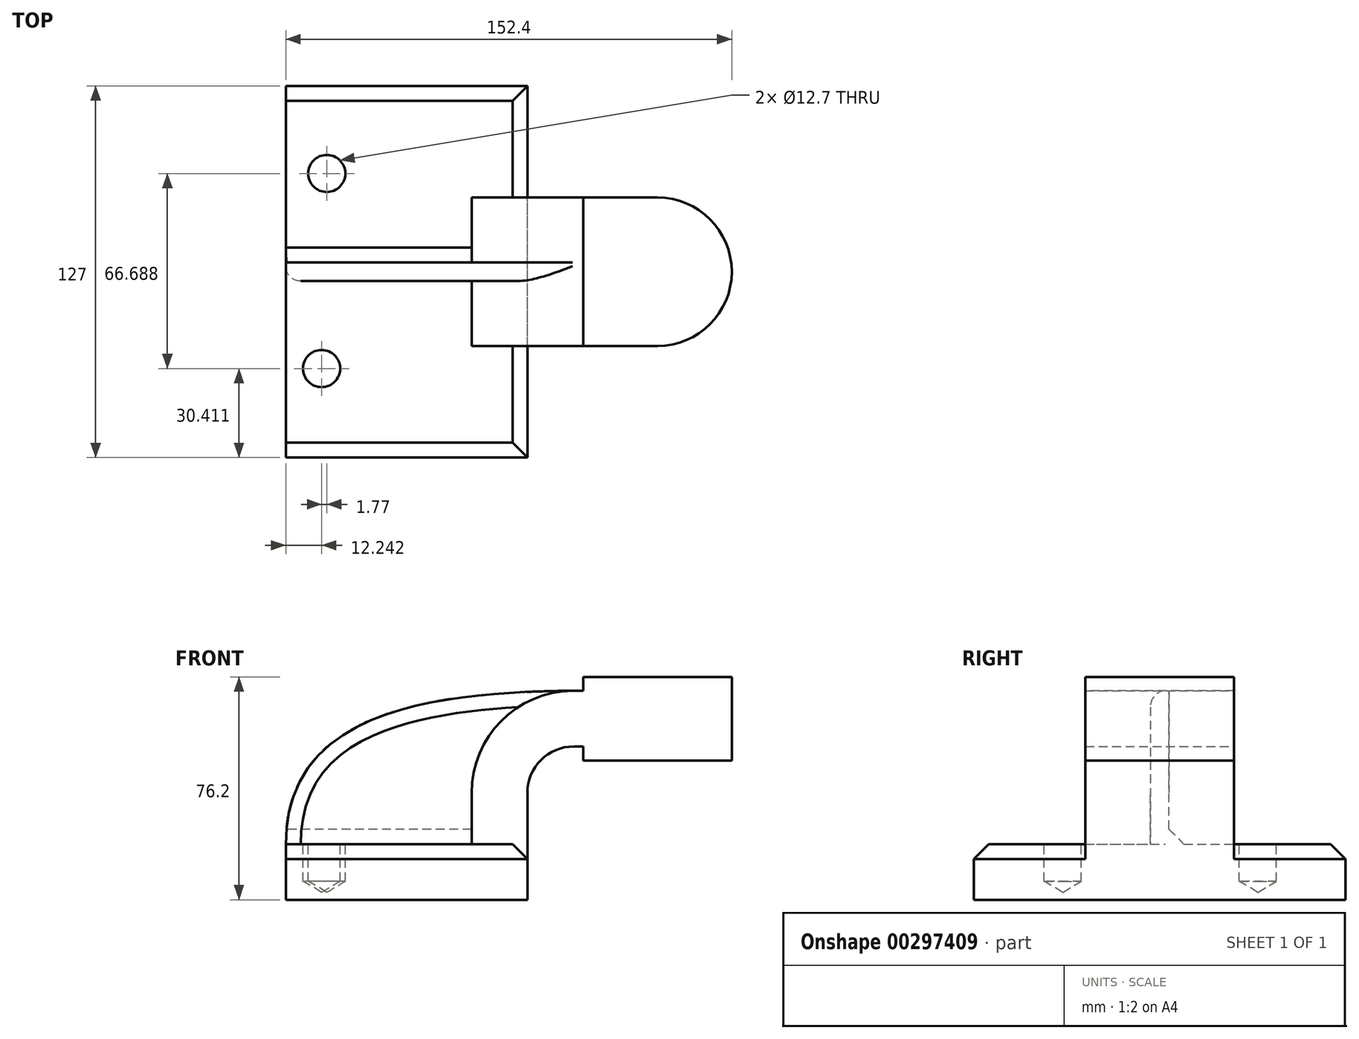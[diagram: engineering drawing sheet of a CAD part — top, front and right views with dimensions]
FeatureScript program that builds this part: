
annotation { "Feature Type Name" : "Feature", "Feature Type Description" : "" }
export const myFeature = defineFeature(function(context is Context, id is Id, definition is map)
    precondition{}
    {
        {
            var Q0;
            Q0=qCreatedBy(makeId("Front.planeOp"),FACE);
            var sketch = newSketch(context, id + "F0", { "sketchPlane" : qUnion([Q0])});
            skLineSegment(sketch, "E0.bottom", {"start": v(41.28, -9.53) * mm, "end": v(-41.27, -9.53) * mm});
            skLineSegment(sketch, "E0.top", {"start": v(41.28, 9.52) * mm, "end": v(-41.28, 9.52) * mm});
            skLineSegment(sketch, "E0.left", {"start": v(41.28, -9.53) * mm, "end": v(41.28, 9.52) * mm});
            skLineSegment(sketch, "E0.right", {"start": v(-41.27, -9.53) * mm, "end": v(-41.27, 9.52) * mm});
            skPoint(sketch, "E0.middle", {"position": v(0, 0) * mm});
            skLineSegment(sketch, "E1.bottom", {"start": v(111.12, 38.1) * mm, "end": v(60.33, 38.1) * mm});
            skLineSegment(sketch, "E1.top", {"start": v(111.12, 66.67) * mm, "end": v(60.33, 66.67) * mm});
            skLineSegment(sketch, "E1.left", {"start": v(111.12, 38.1) * mm, "end": v(111.12, 66.67) * mm});
            skLineSegment(sketch, "E1.right", {"start": v(60.33, 38.1) * mm, "end": v(60.33, 66.67) * mm});
            skPoint(sketch, "E1.middle", {"position": v(85.72, 52.39) * mm});
            skLineSegment(sketch, "E2", {"start": v(41.28, 9.52) * mm, "end": v(41.28, 27) * mm});
            skArc(sketch, "E3", {"start": v(41.28, 27) * mm, "mid": v(45.92, 38.23) * mm, "end": v(57.15, 42.88) * mm});
            skLineSegment(sketch, "E4", {"start": v(57.15, 42.88) * mm, "end": v(85.73, 42.88) * mm});
            skLineSegment(sketch, "E5.0", {"start": v(57.15, 61.93) * mm, "end": v(85.73, 61.93) * mm});
            skArc(sketch, "E5.1", {"start": v(22.23, 27) * mm, "mid": v(32.45, 51.7) * mm, "end": v(57.15, 61.93) * mm});
            skLineSegment(sketch, "E5.2", {"start": v(22.23, 9.52) * mm, "end": v(22.23, 27) * mm});
            skLineSegment(sketch, "E6", {"start": v(85.72, 38.1) * mm, "end": v(85.72, 66.67) * mm});
            skFitSpline(sketch, "E7", {"points": [v(-41.27, 9.52) * mm, v(57.15, 61.93) * mm], "startDerivative": vector(0.8, 125.85) * mm, "endDerivative": vector(171.45, 1.14) * mm});
            skSolve(sketch);
        }
        {
            var Q0;
            Q0=makeQuery(id+"F0.imprint","IMPRINT",FACE,{"disambiguationData":[TD([[makeQuery(id+"F0.imprint","IMPRINT",EDGE,{"derivedFrom":sQuery(id+"F0.wireOp",EDGE,"E0.bottom")}),-1.0]])]});
            extrude(context, id + "F1", {"entities" : qUnion([Q0]), "endBound" : BoundingType.SYMMETRIC, "depth" : 127 * mm});
        }
        {
            var Q0;
            {var subQ1=sQuery(id+"F0.wireOp",EDGE,"E2");Q0=makeQuery(id+"F0.imprint","IMPRINT",FACE,{"disambiguationData":[TD([[makeQuery(id+"F0.imprint","IMPRINT",EDGE,{"derivedFrom":subQ1}),1.0]])]});}
            var Q1;
            {var subQ0=sQuery(id+"F0.wireOp",EDGE,"E4");var subQ1=sQuery(id+"F0.wireOp",EDGE,"E1.right");var subQ2=makeQuery(id+"F0.imprint","INTERSECT",VERTEX,{"derivedFrom":[subQ1,subQ0]});Q1=makeQuery(id+"F0.imprint","IMPRINT",FACE,{"disambiguationData":[TD([[makeQuery(id+"F0.imprint","IMPRINT",EDGE,{"disambiguationData":[TD([[subQ2,-1.0]])],"derivedFrom":subQ1}),-1.0]])]});}
            var Q2;
            {var subQ0=sQuery(id+"F0.wireOp",EDGE,"E1.right");var subQ1=sQuery(id+"F0.wireOp",EDGE,"E1.top");var subQ2=makeQuery(id+"F0.imprint","INTERSECT",VERTEX,{"derivedFrom":[subQ1,subQ0]});Q2=makeQuery(id+"F0.imprint","IMPRINT",FACE,{"disambiguationData":[TD([[makeQuery(id+"F0.imprint","IMPRINT",EDGE,{"disambiguationData":[TD([[subQ2,1.0]])],"derivedFrom":subQ1}),1.0]])]});}
            var Q3;
            {var subQ0=sQuery(id+"F0.wireOp",EDGE,"E1.right");var subQ1=sQuery(id+"F0.wireOp",EDGE,"E1.bottom");var subQ2=makeQuery(id+"F0.imprint","INTERSECT",VERTEX,{"derivedFrom":[subQ1,subQ0]});Q3=makeQuery(id+"F0.imprint","IMPRINT",FACE,{"disambiguationData":[TD([[makeQuery(id+"F0.imprint","IMPRINT",EDGE,{"disambiguationData":[TD([[subQ2,1.0]])],"derivedFrom":subQ1}),-1.0]])]});}
            extrude(context, id + "F2", {"entities" : qUnion([Q0, Q1, Q2, Q3]), "operationType" : NewBodyOperationType.ADD, "endBound" : BoundingType.SYMMETRIC, "depth" : 50.8 * mm});
        }
        {
            var Q0;
            {var subQ3=sQuery(id+"F0.wireOp",EDGE,"E5.2");Q0=makeQuery(id+"F0.imprint","IMPRINT",FACE,{"disambiguationData":[TD([[makeQuery(id+"F0.imprint","IMPRINT",EDGE,{"derivedFrom":subQ3}),1.0]])]});}
            extrude(context, id + "F3", {"entities" : qUnion([Q0]), "operationType" : NewBodyOperationType.ADD, "endBound" : BoundingType.SYMMETRIC, "depth" : 6.35 * mm});
        }
        {
            var Q0;
            {var subQ0=sQuery(id+"F0.wireOp",EDGE,"E1.left");Q0=makeQuery(id+"F0.imprint","IMPRINT",FACE,{"disambiguationData":[TD([[makeQuery(id+"F0.imprint","IMPRINT",EDGE,{"derivedFrom":subQ0}),1.0]])]});}
            var Q1;
            Q1=sQuery(id+"F0.wireOp",EDGE,"E6");
            revolve(context, id + "F4", {"operationType" : NewBodyOperationType.ADD, "entities" : qUnion([Q0]), "axis" : qUnion([Q1]), "revolveType" : RevolveType.FULL});
        }
        {
            var Q0;
            Q0=makeQuery(id+"F3.opExtrude","CAP_EDGE",EDGE,{"disambiguationData":[OSD([sQuery(id+"F0.wireOp",EDGE,"E0.top")])],"isStart":false});
            var Q1;
            Q1=makeQuery(id+"F3.opExtrude","CAP_EDGE",EDGE,{"disambiguationData":[OSD([sQuery(id+"F0.wireOp",EDGE,"E0.top")])],"isStart":true});
            var Q2;
            Q2=makeQuery(id+"F1.opExtrude","CAP_EDGE",EDGE,{"disambiguationData":[OSD([sQuery(id+"F0.wireOp",EDGE,"E0.top")])],"isStart":true});
            var Q3;
            Q3=makeQuery(id+"F1.opExtrude","CAP_EDGE",EDGE,{"disambiguationData":[OSD([sQuery(id+"F0.wireOp",EDGE,"E0.top")])],"isStart":false});
            var Q4;
            {var subQ0=sQuery(id+"F0.wireOp",EDGE,"E0.left");var subQ1=sQuery(id+"F0.wireOp",EDGE,"E2");var subQ2=sQuery(id+"F0.wireOp",EDGE,"E0.top");Q4=makeQuery(id+"F2.boolean.opBoolean","SPLIT",EDGE,{"disambiguationData":[TD([makeQuery(id+"F1.opExtrude","CAP_FACE",FACE,{"disambiguationData":[OSD([sQuery(id+"F0.wireOp",EDGE,"E0.bottom"),subQ2,subQ0,sQuery(id+"F0.wireOp",EDGE,"E0.right")])],"isStart":false})])],"derivedFrom":makeQuery(id+"F1.opExtrude","SWEPT_EDGE",EDGE,{"disambiguationData":[OSD([subQ2,subQ0,subQ1])]})});}
            var Q5;
            {var subQ0=sQuery(id+"F0.wireOp",EDGE,"E2");var subQ1=sQuery(id+"F0.wireOp",EDGE,"E0.top");var subQ2=sQuery(id+"F0.wireOp",EDGE,"E0.left");Q5=makeQuery(id+"F2.boolean.opBoolean","SPLIT",EDGE,{"disambiguationData":[TD([makeQuery(id+"F1.opExtrude","CAP_FACE",FACE,{"disambiguationData":[OSD([sQuery(id+"F0.wireOp",EDGE,"E0.bottom"),subQ1,subQ2,sQuery(id+"F0.wireOp",EDGE,"E0.right")])],"isStart":true})])],"derivedFrom":makeQuery(id+"F1.opExtrude","SWEPT_EDGE",EDGE,{"disambiguationData":[OSD([subQ1,subQ2,subQ0])]})});}
            chamfer(context, id + "F5", {"entities" : qUnion([Q0, Q1, Q2, Q3, Q4, Q5]), "width" : 5.08 * mm, "tangentPropagation" : true});
        }
        {
            var Q0;
            Q0=makeQuery(id+"F3.opExtrude","CAP_EDGE",EDGE,{"disambiguationData":[OSD([sQuery(id+"F0.wireOp",EDGE,"E7")])],"isStart":false});
            fillet(context, id + "F6", {"entities" : qUnion([Q0]), "radius" : 5.08 * mm, "tangentPropagation" : true, "allowEdgeOverflow" : false});
        }
        {
            var Q0;
            {var subQ4=sQuery(id+"F0.wireOp",EDGE,"E0.top");var subQ5=sQuery(id+"F0.wireOp",EDGE,"E0.right");var subQ6=sQuery(id+"F0.wireOp",EDGE,"E0.left");Q0=makeQuery(id+"F3.boolean.opBoolean","SPLIT",FACE,{"disambiguationData":[TD([makeQuery(id+"F1.opExtrude","CAP_FACE",FACE,{"disambiguationData":[OSD([sQuery(id+"F0.wireOp",EDGE,"E0.bottom"),subQ4,subQ6,subQ5])],"isStart":false})])],"derivedFrom":makeQuery(id+"F1.opExtrude","SWEPT_FACE",FACE,{"disambiguationData":[OSD([subQ4])]})});}
            var sketch = newSketch(context, id + "F7", { "sketchPlane" : qUnion([Q0])});
            skCircle(sketch, "E8", {"center": v(-29.04, -33.09) * mm, "radius": 7.03 * mm});
            skSolve(sketch);
        }
        {
            var Q0;
            {var subQ4=sQuery(id+"F0.wireOp",EDGE,"E0.top");var subQ5=sQuery(id+"F0.wireOp",EDGE,"E0.right");var subQ6=sQuery(id+"F0.wireOp",EDGE,"E0.left");Q0=makeQuery(id+"F3.boolean.opBoolean","SPLIT",FACE,{"disambiguationData":[TD([makeQuery(id+"F1.opExtrude","CAP_FACE",FACE,{"disambiguationData":[OSD([sQuery(id+"F0.wireOp",EDGE,"E0.bottom"),subQ4,subQ6,subQ5])],"isStart":true})])],"derivedFrom":makeQuery(id+"F1.opExtrude","SWEPT_FACE",FACE,{"disambiguationData":[OSD([subQ4])]})});}
            var sketch = newSketch(context, id + "F8", { "sketchPlane" : qUnion([Q0])});
            skCircle(sketch, "E9", {"center": v(-27.27, 33.6) * mm, "radius": 6.77 * mm});
            skSolve(sketch);
        }
        {
            var Q0;
            Q0=sQuery(id+"F8.wireOp",VERTEX,"E9.center");
            var Q1;
            Q1=makeQuery(id+"F1.opExtrude","SWEPT_BODY",BODY,{"disambiguationData":[OSD([sQuery(id+"F0.wireOp",EDGE,"E0.bottom"),sQuery(id+"F0.wireOp",EDGE,"E0.top"),sQuery(id+"F0.wireOp",EDGE,"E0.left"),sQuery(id+"F0.wireOp",EDGE,"E0.right")])]});
            hole(context, id + "F9", {"style" : HoleStyle.C_SINK, "endStyle" : HoleEndStyle.BLIND, "holeDiameter" : 12.7 * mm, "cSinkDiameter" : 12.7 * mm, "cSinkAngle" : 90 * degree, "holeDepth" : 12.7 * mm, "tappedDepth" : 12.7 * mm, "tapClearance" : 3, "locations" : qUnion([Q0]), "scope" : qUnion([Q1])});
        }
        {
            var Q0;
            Q0=sQuery(id+"F7.wireOp",VERTEX,"E8.center");
            var Q1;
            Q1=makeQuery(id+"F1.opExtrude","SWEPT_BODY",BODY,{"disambiguationData":[OSD([sQuery(id+"F0.wireOp",EDGE,"E0.bottom"),sQuery(id+"F0.wireOp",EDGE,"E0.top"),sQuery(id+"F0.wireOp",EDGE,"E0.left"),sQuery(id+"F0.wireOp",EDGE,"E0.right")])]});
            hole(context, id + "F10", {"style" : HoleStyle.C_SINK, "endStyle" : HoleEndStyle.BLIND, "holeDiameter" : 12.7 * mm, "cSinkDiameter" : 12.7 * mm, "cSinkAngle" : 90 * degree, "holeDepth" : 12.7 * mm, "tappedDepth" : 12.7 * mm, "tapClearance" : 3, "locations" : qUnion([Q0]), "scope" : qUnion([Q1])});
        }
    });
